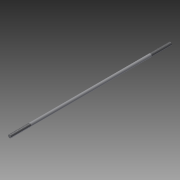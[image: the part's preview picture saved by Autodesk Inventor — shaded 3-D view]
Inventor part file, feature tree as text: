
AUTODESK INVENTOR PART (.ipt)
format: ipt  version: 2015 (Build 190159000, 159)  size: 69,632 bytes
history: native  units: mm
features: thread x2, extrude x1, sketch x1
ambient origin geometry x8: Origin, YZ Plane, XZ Plane, XY Plane, X Axis, Y Axis, Z Axis, Center Point
bodies: Solid1 (feature_tree)
feature tree (4):
  extrude  "Extrusion1"  Depth=160.0mm TaperAngle=0.0deg
  thread  "Thread1"  [1 undecoded]
  thread  "Thread2"  [1 undecoded]
  sketch  "Sketch1"  dims[d0=3.0mm d1=160.0mm d2=0.0mm d3=20.0mm d4=0.0mm d5=20.0mm d6=0.0mm]
note: 2 required parameter values undecoded (feature->parameter linkage not recoverable at this tier; creation-order binding heuristic only, values carry confidence <= 0.55)
